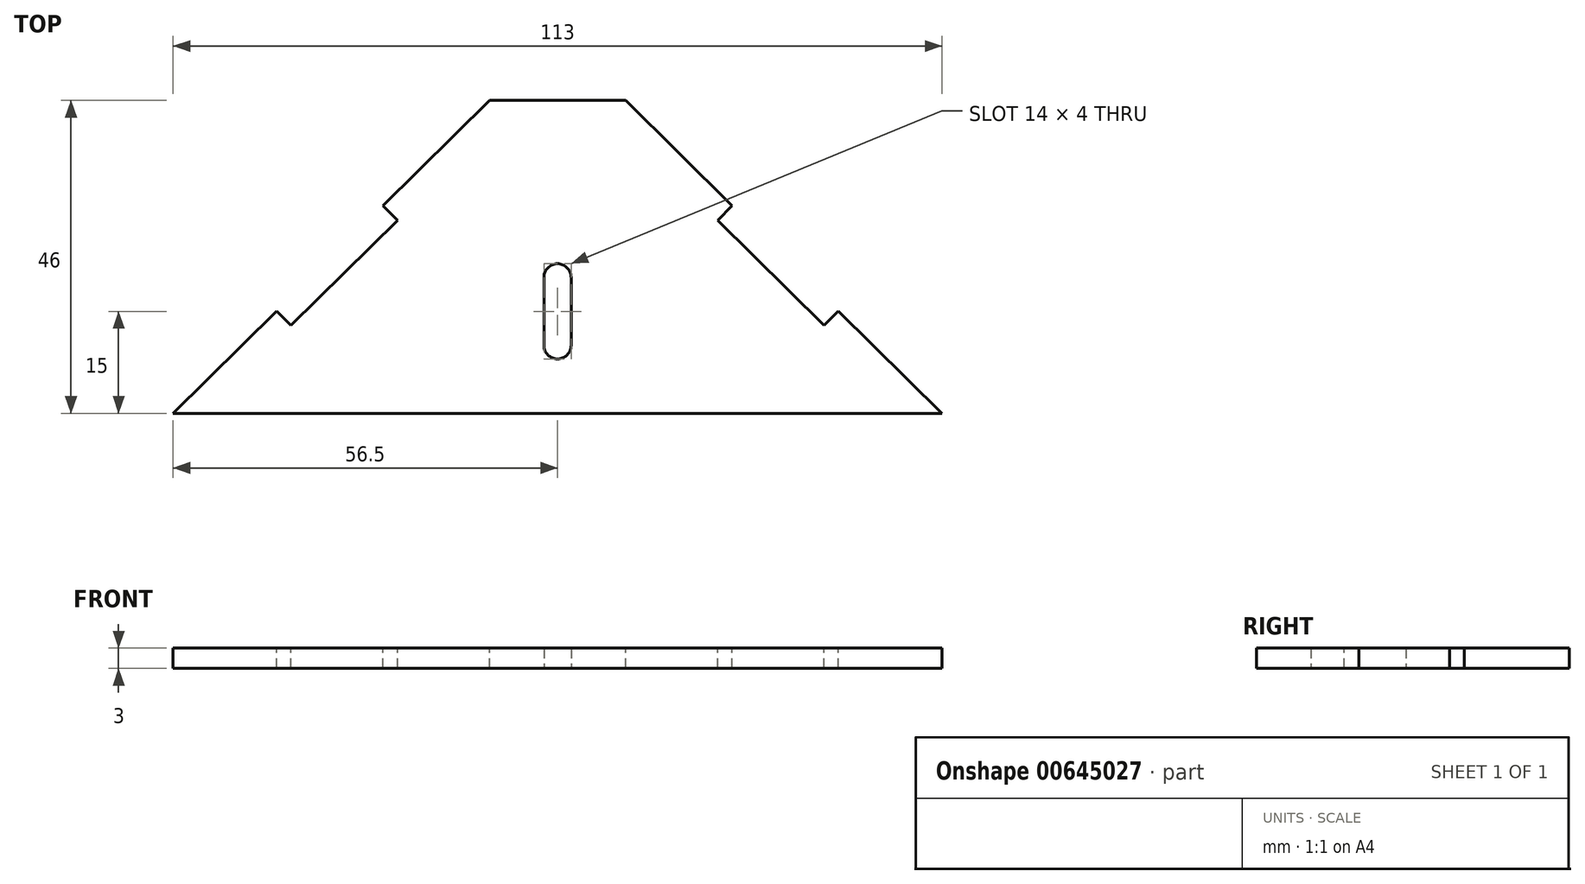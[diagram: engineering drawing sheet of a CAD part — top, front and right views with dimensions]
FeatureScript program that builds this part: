
annotation { "Feature Type Name" : "Feature", "Feature Type Description" : "" }
export const myFeature = defineFeature(function(context is Context, id is Id, definition is map)
    precondition{}
    {
        {
            var Q0;
            Q0=qCreatedBy(makeId("Front.planeOp"),FACE);
            var sketch = newSketch(context, id + "F0", { "sketchPlane" : qUnion([Q0])});
            skLineSegment(sketch, "E0", {"start": v(46.5, 46) * mm, "end": v(66.5, 46) * mm});
            skLineSegment(sketch, "E1", {"start": v(0, 0) * mm, "end": v(113, 0) * mm});
            skLineSegment(sketch, "E2", {"start": v(46.5, 46) * mm, "end": v(30.86, 30.53) * mm});
            skLineSegment(sketch, "E3", {"start": v(15.22, 15.06) * mm, "end": v(17.33, 12.92) * mm});
            skLineSegment(sketch, "E4", {"start": v(17.33, 12.92) * mm, "end": v(32.97, 28.4) * mm});
            skLineSegment(sketch, "E5", {"start": v(32.97, 28.4) * mm, "end": v(30.86, 30.53) * mm});
            skLineSegment(sketch, "E6", {"start": v(15.22, 15.06) * mm, "end": v(0, 0) * mm});
            skLineSegment(sketch, "E7", {"start": v(66.5, 46) * mm, "end": v(82.14, 30.53) * mm});
            skLineSegment(sketch, "E8", {"start": v(97.78, 15.06) * mm, "end": v(95.67, 12.92) * mm});
            skLineSegment(sketch, "E9", {"start": v(95.67, 12.92) * mm, "end": v(80.03, 28.4) * mm});
            skLineSegment(sketch, "E10", {"start": v(80.03, 28.4) * mm, "end": v(82.14, 30.53) * mm});
            skLineSegment(sketch, "E11", {"start": v(97.78, 15.06) * mm, "end": v(113, 0) * mm});
            skSolve(sketch);
        }
        {
            var Q0;
            Q0 = qSketchRegion(id + "F0", true);
            extrude(context, id + "F1", {"entities" : qUnion([Q0]), "depth" : 3 * mm, "offsetDistance" : 25 * mm});
        }
        {
            var Q0;
            Q0=makeQuery(id+"F1.opExtrude","CAP_FACE",FACE,{"disambiguationData":[OSD([sQuery(id+"F0.wireOp",EDGE,"E0"),sQuery(id+"F0.wireOp",EDGE,"E1"),sQuery(id+"F0.wireOp",EDGE,"E2"),sQuery(id+"F0.wireOp",EDGE,"E3"),sQuery(id+"F0.wireOp",EDGE,"E4"),sQuery(id+"F0.wireOp",EDGE,"E5"),sQuery(id+"F0.wireOp",EDGE,"E6"),sQuery(id+"F0.wireOp",EDGE,"E7"),sQuery(id+"F0.wireOp",EDGE,"E8"),sQuery(id+"F0.wireOp",EDGE,"E9"),sQuery(id+"F0.wireOp",EDGE,"E10"),sQuery(id+"F0.wireOp",EDGE,"E11")])],"isStart":false});
            var sketch = newSketch(context, id + "F2", { "sketchPlane" : qUnion([Q0])});
            skLineSegment(sketch, "E12.right", {"start": v(58.5, 19.63) * mm, "end": v(58.5, 20) * mm});
            skLineSegment(sketch, "E13.left", {"start": v(58.5, 20) * mm, "end": v(58.5, 10) * mm});
            skLineSegment(sketch, "E13.right", {"start": v(54.5, 20) * mm, "end": v(54.5, 10) * mm});
            skArc(sketch, "E14", {"start": v(58.5, 20) * mm, "mid": v(56.5, 22) * mm, "end": v(54.5, 20) * mm});
            skArc(sketch, "E15", {"start": v(54.5, 10) * mm, "mid": v(56.5, 8) * mm, "end": v(58.5, 10) * mm});
            skSolve(sketch);
        }
        {
            var Q0;
            Q0=makeQuery(id+"F2.imprint","IMPRINT",FACE,{"disambiguationData":[TD([[makeQuery(id+"F2.imprint","IMPRINT",EDGE,{"derivedFrom":sQuery(id+"F2.wireOp",EDGE,"E13.right")}),1.0]])]});
            extrude(context, id + "F3", {"entities" : qUnion([Q0]), "operationType" : NewBodyOperationType.REMOVE, "oppositeDirection" : true, "depth" : 25 * mm, "offsetDistance" : 25 * mm});
        }
        {
            var Q0;
            Q0=makeQuery(id+"F1.opExtrude","SWEPT_BODY",BODY,{"disambiguationData":[OSD([sQuery(id+"F0.wireOp",EDGE,"E0"),sQuery(id+"F0.wireOp",EDGE,"E1"),sQuery(id+"F0.wireOp",EDGE,"E2"),sQuery(id+"F0.wireOp",EDGE,"E3"),sQuery(id+"F0.wireOp",EDGE,"E4"),sQuery(id+"F0.wireOp",EDGE,"E5"),sQuery(id+"F0.wireOp",EDGE,"E6"),sQuery(id+"F0.wireOp",EDGE,"E7"),sQuery(id+"F0.wireOp",EDGE,"E8"),sQuery(id+"F0.wireOp",EDGE,"E9"),sQuery(id+"F0.wireOp",EDGE,"E10"),sQuery(id+"F0.wireOp",EDGE,"E11")])]});
            var Q1;
            Q1=makeQuery(id+"F1.opExtrude","CAP_EDGE",EDGE,{"disambiguationData":[OSD([sQuery(id+"F0.wireOp",EDGE,"E1")])],"isStart":false});
            transform(context, id + "F4", {"entities" : qUnion([Q0]), "transformType" : TransformType.ROTATION, "transformAxis" : qUnion([Q1]), "angle" : 90 * degree, "makeCopy" : false});
        }
        {
            var Q0;
            Q0=makeQuery(id+"F1.opExtrude","SWEPT_BODY",BODY,{"disambiguationData":[OSD([sQuery(id+"F0.wireOp",EDGE,"E0"),sQuery(id+"F0.wireOp",EDGE,"E1"),sQuery(id+"F0.wireOp",EDGE,"E2"),sQuery(id+"F0.wireOp",EDGE,"E3"),sQuery(id+"F0.wireOp",EDGE,"E4"),sQuery(id+"F0.wireOp",EDGE,"E5"),sQuery(id+"F0.wireOp",EDGE,"E6"),sQuery(id+"F0.wireOp",EDGE,"E7"),sQuery(id+"F0.wireOp",EDGE,"E8"),sQuery(id+"F0.wireOp",EDGE,"E9"),sQuery(id+"F0.wireOp",EDGE,"E10"),sQuery(id+"F0.wireOp",EDGE,"E11")])]});
            var Q1;
            Q1=makeQuery(id+"F1.opExtrude","SWEPT_EDGE",EDGE,{"disambiguationData":[OSD([sQuery(id+"F0.wireOp",EDGE,"E1"),sQuery(id+"F0.wireOp",EDGE,"E6")])]});
            transform(context, id + "F5", {"entities" : qUnion([Q0]), "transformType" : TransformType.ROTATION, "transformAxis" : qUnion([Q1]), "angle" : 180 * degree, "oppositeDirection" : true, "makeCopy" : false});
        }
    });
